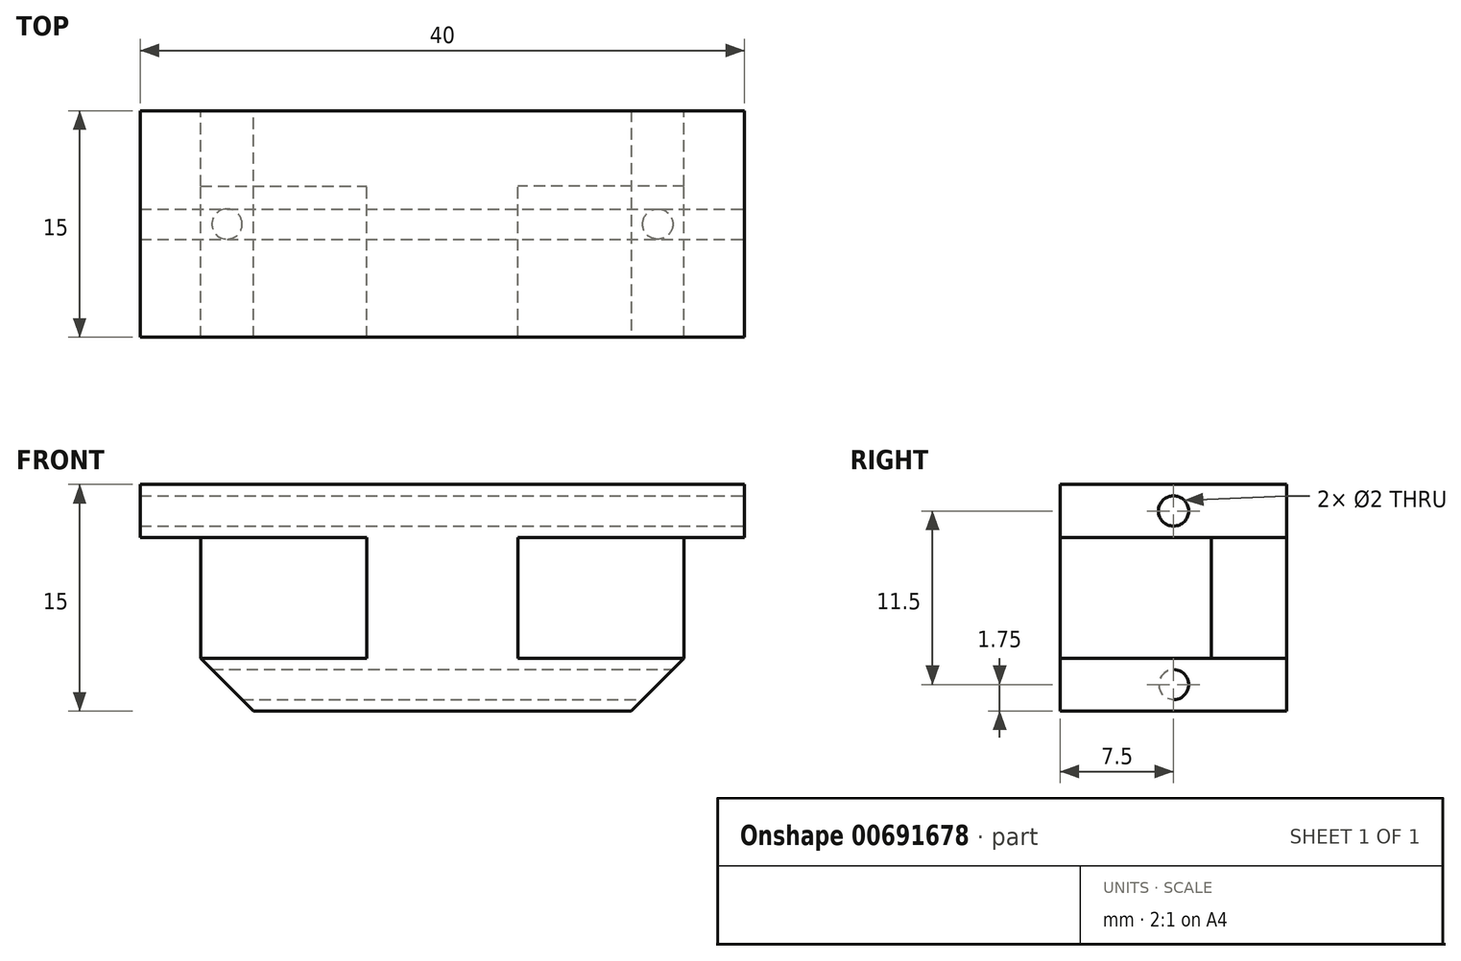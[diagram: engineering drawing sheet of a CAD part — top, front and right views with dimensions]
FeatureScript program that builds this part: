
annotation { "Feature Type Name" : "Feature", "Feature Type Description" : "" }
export const myFeature = defineFeature(function(context is Context, id is Id, definition is map)
    precondition{}
    {
        {
            var Q0;
            Q0=qCreatedBy(makeId("Front.planeOp"),FACE);
            var sketch = newSketch(context, id + "F0", { "sketchPlane" : qUnion([Q0])});
            skLineSegment(sketch, "E0.bottom", {"start": v(5, 4) * mm, "end": v(-5, 4) * mm});
            skLineSegment(sketch, "E0.top", {"start": v(5, -4) * mm, "end": v(-5, -4) * mm});
            skLineSegment(sketch, "E0.left", {"start": v(5, 4) * mm, "end": v(5, -4) * mm});
            skLineSegment(sketch, "E0.right", {"start": v(-5, 4) * mm, "end": v(-5, -4) * mm});
            skPoint(sketch, "E0.middle", {"position": v(0, 0) * mm});
            skLineSegment(sketch, "E1.bottom", {"start": v(-5, 4) * mm, "end": v(-20, 4) * mm});
            skLineSegment(sketch, "E1.top", {"start": v(-5, -4) * mm, "end": v(-20, -4) * mm});
            skLineSegment(sketch, "E1.right", {"start": v(-20, 4) * mm, "end": v(-20, -4) * mm});
            skLineSegment(sketch, "E2.bottom", {"start": v(5, 4) * mm, "end": v(20, 4) * mm});
            skLineSegment(sketch, "E2.top", {"start": v(5, -4) * mm, "end": v(20, -4) * mm});
            skLineSegment(sketch, "E2.right", {"start": v(20, 4) * mm, "end": v(20, -4) * mm});
            skLineSegment(sketch, "E3.bottom", {"start": v(-20, 4) * mm, "end": v(20, 4) * mm});
            skLineSegment(sketch, "E3.top", {"start": v(-20, 7.5) * mm, "end": v(20, 7.5) * mm});
            skLineSegment(sketch, "E3.left", {"start": v(-20, 4) * mm, "end": v(-20, 7.5) * mm});
            skLineSegment(sketch, "E3.right", {"start": v(20, 4) * mm, "end": v(20, 7.5) * mm});
            skLineSegment(sketch, "E4.bottom", {"start": v(-16, 0) * mm, "end": v(16, 0) * mm});
            skLineSegment(sketch, "E4.top", {"start": v(-16, -7.5) * mm, "end": v(16, -7.5) * mm});
            skLineSegment(sketch, "E4.left", {"start": v(-16, 0) * mm, "end": v(-16, -7.5) * mm});
            skLineSegment(sketch, "E4.right", {"start": v(16, 0) * mm, "end": v(16, -7.5) * mm});
            skLineSegment(sketch, "E5.bottom", {"start": v(5, 4) * mm, "end": v(16, 4) * mm});
            skLineSegment(sketch, "E5.top", {"start": v(5, -4) * mm, "end": v(16, -4) * mm});
            skLineSegment(sketch, "E5.right", {"start": v(16, 4) * mm, "end": v(16, -4) * mm});
            skLineSegment(sketch, "E6.bottom", {"start": v(-5, 4) * mm, "end": v(-16, 4) * mm});
            skLineSegment(sketch, "E6.top", {"start": v(-5, -4) * mm, "end": v(-16, -4) * mm});
            skLineSegment(sketch, "E6.right", {"start": v(-16, 4) * mm, "end": v(-16, -4) * mm});
            skSolve(sketch);
        }
        {
            var Q0;
            {var subQ0=sQuery(id+"F0.wireOp",EDGE,"E3.bottom");var subQ1=sQuery(id+"F0.wireOp",EDGE,"E0.right");var subQ2=makeQuery(id+"F0.imprint","INTERSECT",VERTEX,{"derivedFrom":[subQ1,subQ0]});Q0=makeQuery(id+"F0.imprint","IMPRINT",FACE,{"disambiguationData":[TD([[makeQuery(id+"F0.imprint","IMPRINT",EDGE,{"disambiguationData":[TD([[subQ2,-1.0]])],"derivedFrom":subQ1}),1.0]])]});}
            var Q1;
            {var subQ0=sQuery(id+"F0.wireOp",EDGE,"E0.top");Q1=makeQuery(id+"F0.imprint","IMPRINT",FACE,{"disambiguationData":[TD([[makeQuery(id+"F0.imprint","IMPRINT",EDGE,{"derivedFrom":subQ0}),-1.0]])]});}
            var Q2;
            {var subQ2=sQuery(id+"F0.wireOp",EDGE,"E0.top");Q2=makeQuery(id+"F0.imprint","IMPRINT",FACE,{"disambiguationData":[TD([[makeQuery(id+"F0.imprint","IMPRINT",EDGE,{"derivedFrom":subQ2}),1.0]])]});}
            var Q3;
            {var subQ5=sQuery(id+"F0.wireOp",EDGE,"E0.bottom");Q3=makeQuery(id+"F0.imprint","IMPRINT",FACE,{"disambiguationData":[TD([[makeQuery(id+"F0.imprint","IMPRINT",EDGE,{"derivedFrom":subQ5}),-1.0]])]});}
            var Q4;
            {var subQ1=sQuery(id+"F0.wireOp",EDGE,"E0.left");var subQ2=sQuery(id+"F0.wireOp",EDGE,"E0.top");var subQ4=sQuery(id+"F0.wireOp",EDGE,"E4.bottom");var subQ5=makeQuery(id+"F0.imprint","INTERSECT",VERTEX,{"derivedFrom":[subQ1,subQ4]});var subQ6=makeQuery(id+"F0.imprint","IMPRINT",EDGE,{"disambiguationData":[TD([[subQ5,-1.0]])],"derivedFrom":subQ1});var subQ11=sQuery(id+"F0.wireOp",EDGE,"E0.right");var subQ13=makeQuery(id+"F0.imprint","INTERSECT",VERTEX,{"derivedFrom":[subQ11,subQ4]});var subQ14=makeQuery(id+"F0.imprint","IMPRINT",EDGE,{"disambiguationData":[TD([[subQ13,-1.0]])],"derivedFrom":subQ11});Q4=qUnion([makeQuery(id+"F0.imprint","IMPRINT",FACE,{"disambiguationData":[TD([[makeQuery(id+"F0.imprint","IMPRINT",EDGE,{"derivedFrom":subQ2}),-1.0]])]}),makeQuery(id+"F0.imprint","IMPRINT",FACE,{"disambiguationData":[TD([[subQ14,-1.0]])]}),makeQuery(id+"F0.imprint","IMPRINT",FACE,{"disambiguationData":[TD([[subQ6,1.0]])]})]);}
            var Q5;
            {var subQ1=sQuery(id+"F0.wireOp",EDGE,"E0.left");var subQ2=sQuery(id+"F0.wireOp",EDGE,"E0.top");var subQ4=sQuery(id+"F0.wireOp",EDGE,"E4.bottom");var subQ5=makeQuery(id+"F0.imprint","INTERSECT",VERTEX,{"derivedFrom":[subQ1,subQ4]});var subQ6=makeQuery(id+"F0.imprint","IMPRINT",EDGE,{"disambiguationData":[TD([[subQ5,-1.0]])],"derivedFrom":subQ1});var subQ11=sQuery(id+"F0.wireOp",EDGE,"E0.right");var subQ13=makeQuery(id+"F0.imprint","INTERSECT",VERTEX,{"derivedFrom":[subQ11,subQ4]});var subQ14=makeQuery(id+"F0.imprint","IMPRINT",EDGE,{"disambiguationData":[TD([[subQ13,-1.0]])],"derivedFrom":subQ11});Q5=qUnion([makeQuery(id+"F0.imprint","IMPRINT",FACE,{"disambiguationData":[TD([[makeQuery(id+"F0.imprint","IMPRINT",EDGE,{"derivedFrom":subQ2}),-1.0]])]}),makeQuery(id+"F0.imprint","IMPRINT",FACE,{"disambiguationData":[TD([[subQ14,-1.0]])]}),makeQuery(id+"F0.imprint","IMPRINT",FACE,{"disambiguationData":[TD([[subQ6,1.0]])]})]);}
            var Q6;
            {var subQ5=sQuery(id+"F0.wireOp",EDGE,"E5.right");Q6=makeQuery(id+"F0.imprint","IMPRINT",FACE,{"disambiguationData":[TD([[makeQuery(id+"F0.imprint","IMPRINT",EDGE,{"derivedFrom":subQ5}),-1.0]])]});}
            var Q7;
            {var subQ0=sQuery(id+"F0.wireOp",EDGE,"E0.bottom");Q7=makeQuery(id+"F0.imprint","IMPRINT",FACE,{"disambiguationData":[TD([[makeQuery(id+"F0.imprint","IMPRINT",EDGE,{"derivedFrom":subQ0}),1.0]])]});}
            var Q8;
            {var subQ5=sQuery(id+"F0.wireOp",EDGE,"E6.right");Q8=makeQuery(id+"F0.imprint","IMPRINT",FACE,{"disambiguationData":[TD([[makeQuery(id+"F0.imprint","IMPRINT",EDGE,{"derivedFrom":subQ5}),1.0]])]});}
            extrude(context, id + "F1", {"entities" : qUnion([Q0, Q1, Q2, Q3, Q4, Q5, Q6, Q7, Q8]), "depth" : 5 * mm, "offsetDistance" : 25 * mm});
        }
        {
            var Q0;
            {var subQ5=sQuery(id+"F0.wireOp",EDGE,"E0.bottom");Q0=makeQuery(id+"F0.imprint","IMPRINT",FACE,{"disambiguationData":[TD([[makeQuery(id+"F0.imprint","IMPRINT",EDGE,{"derivedFrom":subQ5}),-1.0]])]});}
            var Q1;
            {var subQ0=sQuery(id+"F0.wireOp",EDGE,"E0.bottom");Q1=makeQuery(id+"F0.imprint","IMPRINT",FACE,{"disambiguationData":[TD([[makeQuery(id+"F0.imprint","IMPRINT",EDGE,{"derivedFrom":subQ0}),1.0]])]});}
            var Q2;
            {var subQ0=sQuery(id+"F0.wireOp",EDGE,"E0.top");Q2=makeQuery(id+"F0.imprint","IMPRINT",FACE,{"disambiguationData":[TD([[makeQuery(id+"F0.imprint","IMPRINT",EDGE,{"derivedFrom":subQ0}),-1.0]])]});}
            var Q3;
            {var subQ2=sQuery(id+"F0.wireOp",EDGE,"E0.top");Q3=makeQuery(id+"F0.imprint","IMPRINT",FACE,{"disambiguationData":[TD([[makeQuery(id+"F0.imprint","IMPRINT",EDGE,{"derivedFrom":subQ2}),1.0]])]});}
            extrude(context, id + "F2", {"entities" : qUnion([Q0, Q1, Q2, Q3]), "operationType" : NewBodyOperationType.ADD, "depth" : 15 * mm, "offsetDistance" : 25 * mm});
        }
        {
            var Q0;
            {var subQ0=sQuery(id+"F0.wireOp",EDGE,"E3.right");Q0=makeQuery(id+"F2.boolean.opBoolean","MERGE",FACE,{"derivedFrom":[makeQuery(id+"F1.opExtrude","SWEPT_FACE",FACE,{"disambiguationData":[OSD([subQ0])]}),makeQuery(id+"F2.opExtrude","SWEPT_FACE",FACE,{"disambiguationData":[OSD([subQ0])]})]});}
            var sketch = newSketch(context, id + "F3", { "sketchPlane" : qUnion([Q0])});
            skLineSegment(sketch, "E7", {"start": v(-7.5, 7.5) * mm, "end": v(-7.5, -7.5) * mm});
            skLineSegment(sketch, "E8", {"start": v(-7.5, -7.5) * mm, "end": v(-7.5, -4) * mm});
            skLineSegment(sketch, "E9", {"start": v(-7.5, 7.5) * mm, "end": v(-7.5, 4) * mm});
            skCircle(sketch, "E10", {"center": v(-7.5, -5.75) * mm, "radius": 1 * mm});
            skCircle(sketch, "E11", {"center": v(-7.5, 5.75) * mm, "radius": 1 * mm});
            skSolve(sketch);
        }
        {
            var Q0;
            Q0 = qSketchRegion(id + "F3", true);
            extrude(context, id + "F4", {"entities" : qUnion([Q0]), "operationType" : NewBodyOperationType.REMOVE, "oppositeDirection" : true, "depth" : 40 * mm, "offsetDistance" : 25 * mm});
        }
        {
            var Q0;
            {var subQ0=sQuery(id+"F0.wireOp",EDGE,"E4.left");var subQ1=sQuery(id+"F0.wireOp",EDGE,"E4.top");Q0=makeQuery(id+"F2.boolean.opBoolean","MERGE",EDGE,{"derivedFrom":[makeQuery(id+"F1.opExtrude","SWEPT_EDGE",EDGE,{"disambiguationData":[OSD([subQ1,subQ0])]}),makeQuery(id+"F2.opExtrude","SWEPT_EDGE",EDGE,{"disambiguationData":[OSD([subQ1,subQ0])]})]});}
            var Q1;
            {var subQ0=sQuery(id+"F0.wireOp",EDGE,"E4.right");var subQ1=sQuery(id+"F0.wireOp",EDGE,"E4.top");Q1=makeQuery(id+"F2.boolean.opBoolean","MERGE",EDGE,{"derivedFrom":[makeQuery(id+"F1.opExtrude","SWEPT_EDGE",EDGE,{"disambiguationData":[OSD([subQ1,subQ0])]}),makeQuery(id+"F2.opExtrude","SWEPT_EDGE",EDGE,{"disambiguationData":[OSD([subQ1,subQ0])]})]});}
            chamfer(context, id + "F5", {"entities" : qUnion([Q0, Q1]), "width" : 3.5 * mm, "tangentPropagation" : true});
        }
    });
